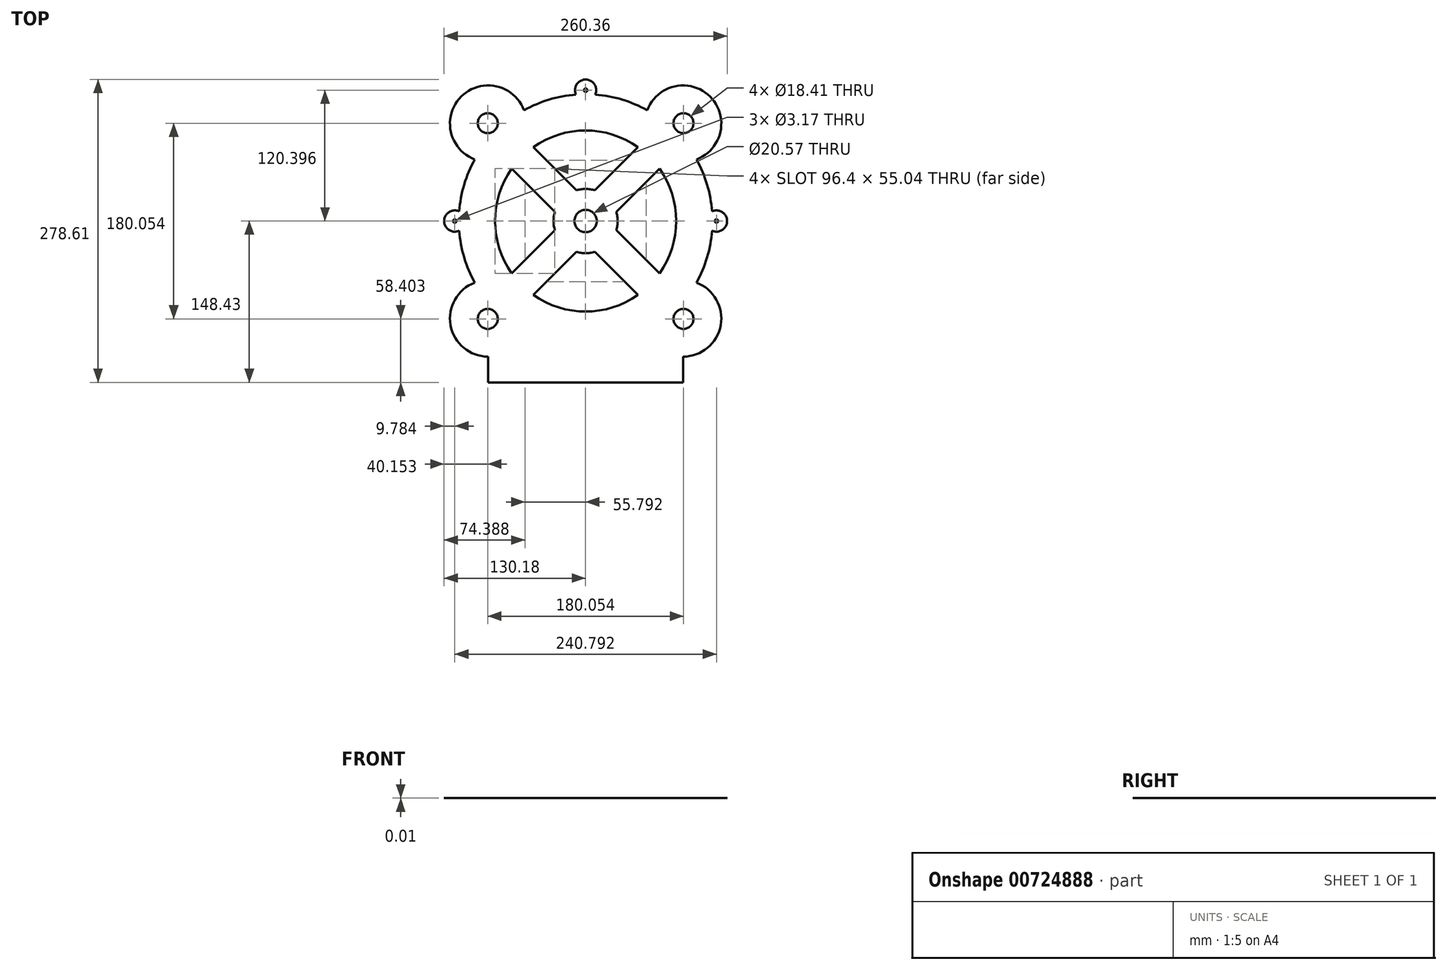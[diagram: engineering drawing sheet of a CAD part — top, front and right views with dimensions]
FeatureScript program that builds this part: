
annotation { "Feature Type Name" : "Feature", "Feature Type Description" : "" }
export const myFeature = defineFeature(function(context is Context, id is Id, definition is map)
    precondition{}
    {
        {
            var Q0;
            Q0=qCreatedBy(makeId("Top.planeOp"),FACE);
            var sketch = newSketch(context, id + "F0", { "sketchPlane" : qUnion([Q0])});
            skCircle(sketch, "E0", {"center": v(0, 0) * mm, "radius": 116.68 * mm});
            skLineSegment(sketch, "E1", {"start": v(0, 0) * mm, "end": v(-122.35, 122.35) * mm});
            skLineSegment(sketch, "E2", {"start": v(0, 0) * mm, "end": v(131.34, 131.34) * mm});
            skLineSegment(sketch, "E3", {"start": v(0, 0) * mm, "end": v(155.82, -155.82) * mm});
            skLineSegment(sketch, "E4", {"start": v(0, 0) * mm, "end": v(-127.24, -127.24) * mm});
            skCircle(sketch, "E5", {"center": v(89.62, 89.62) * mm, "radius": 35.18 * mm});
            skCircle(sketch, "E6", {"center": v(-89.62, -89.62) * mm, "radius": 35.18 * mm});
            skCircle(sketch, "E7", {"center": v(89.62, -89.62) * mm, "radius": 35.18 * mm});
            skCircle(sketch, "E8", {"center": v(-89.62, 89.62) * mm, "radius": 35.18 * mm});
            skCircle(sketch, "E9", {"center": v(0, 120.4) * mm, "radius": 9.78 * mm});
            skCircle(sketch, "E10", {"center": v(120.4, 0) * mm, "radius": 9.78 * mm});
            skCircle(sketch, "E11", {"center": v(-120.4, 0) * mm, "radius": 9.78 * mm});
            skCircle(sketch, "E12", {"center": v(0, 0) * mm, "radius": 10.29 * mm});
            skCircle(sketch, "E13", {"center": v(0, 0) * mm, "radius": 29.53 * mm});
            skCircle(sketch, "E14", {"center": v(-90.03, 90.03) * mm, "radius": 9.2 * mm});
            skCircle(sketch, "E15", {"center": v(90.03, 90.03) * mm, "radius": 9.2 * mm});
            skCircle(sketch, "E16", {"center": v(90.03, -90.03) * mm, "radius": 9.2 * mm});
            skCircle(sketch, "E17", {"center": v(-90.03, -90.03) * mm, "radius": 9.2 * mm});
            skLineSegment(sketch, "E18.0", {"start": v(9.88, 9.88) * mm, "end": v(-48.2, 67.95) * mm});
            skLineSegment(sketch, "E18.1", {"start": v(9.88, 9.88) * mm, "end": v(67.95, -48.2) * mm});
            skLineSegment(sketch, "E19.0", {"start": v(-9.88, -9.88) * mm, "end": v(48.2, -67.95) * mm});
            skLineSegment(sketch, "E19.1", {"start": v(-9.88, -9.88) * mm, "end": v(-67.95, 48.2) * mm});
            skLineSegment(sketch, "E20", {"start": v(-67.95, -48.2) * mm, "end": v(48.2, 67.95) * mm});
            skCircle(sketch, "E21", {"center": v(0, 0) * mm, "radius": 83.31 * mm});
            skLineSegment(sketch, "E22.trimOffspring", {"start": v(-48.2, -67.95) * mm, "end": v(67.95, 48.2) * mm});
            skLineSegment(sketch, "E23", {"start": v(-89.62, -124.8) * mm, "end": v(-89.62, -148.43) * mm});
            skLineSegment(sketch, "E24", {"start": v(-89.62, -148.43) * mm, "end": v(89.62, -148.43) * mm});
            skLineSegment(sketch, "E25", {"start": v(89.62, -148.43) * mm, "end": v(89.62, -124.8) * mm});
            skCircle(sketch, "E26", {"center": v(120.4, 0) * mm, "radius": 1.59 * mm});
            skCircle(sketch, "E27", {"center": v(-120.4, 0) * mm, "radius": 1.59 * mm});
            skCircle(sketch, "E28", {"center": v(0, 120.4) * mm, "radius": 1.59 * mm});
            skSolve(sketch);
        }
        {
            var Q0;
            {var subQ0=sQuery(id+"F0.wireOp",EDGE,"E8");var subQ5=sQuery(id+"F0.wireOp",EDGE,"E0");var subQ6=makeQuery(id+"F0.imprint","INTERSECT",VERTEX,{"disambiguationData":[OD(1.0)],"derivedFrom":[subQ5,subQ0]});Q0=makeQuery(id+"F0.imprint","IMPRINT",FACE,{"disambiguationData":[TD([[makeQuery(id+"F0.imprint","IMPRINT",EDGE,{"disambiguationData":[TD([[subQ6,1.0]])],"derivedFrom":subQ5}),-1.0]])]});}
            var Q1;
            {var subQ0=sQuery(id+"F0.wireOp",EDGE,"E8");var subQ3=sQuery(id+"F0.wireOp",EDGE,"E0");var subQ4=makeQuery(id+"F0.imprint","INTERSECT",VERTEX,{"disambiguationData":[OD(0.0)],"derivedFrom":[subQ3,subQ0]});Q1=makeQuery(id+"F0.imprint","IMPRINT",FACE,{"disambiguationData":[TD([[makeQuery(id+"F0.imprint","IMPRINT",EDGE,{"disambiguationData":[TD([[subQ4,-1.0]])],"derivedFrom":subQ3}),-1.0]])]});}
            var Q2;
            {var subQ0=sQuery(id+"F0.wireOp",EDGE,"E8");var subQ1=sQuery(id+"F0.wireOp",EDGE,"E0");var subQ2=makeQuery(id+"F0.imprint","INTERSECT",VERTEX,{"disambiguationData":[OD(0.0)],"derivedFrom":[subQ1,subQ0]});Q2=makeQuery(id+"F0.imprint","IMPRINT",FACE,{"disambiguationData":[TD([[makeQuery(id+"F0.imprint","IMPRINT",EDGE,{"disambiguationData":[TD([[subQ2,-1.0]])],"derivedFrom":subQ1}),1.0]])]});}
            var Q3;
            {var subQ0=sQuery(id+"F0.wireOp",EDGE,"E8");var subQ1=sQuery(id+"F0.wireOp",EDGE,"E0");var subQ2=makeQuery(id+"F0.imprint","INTERSECT",VERTEX,{"disambiguationData":[OD(1.0)],"derivedFrom":[subQ1,subQ0]});Q3=makeQuery(id+"F0.imprint","IMPRINT",FACE,{"disambiguationData":[TD([[makeQuery(id+"F0.imprint","IMPRINT",EDGE,{"disambiguationData":[TD([[subQ2,1.0]])],"derivedFrom":subQ1}),1.0]])]});}
            var Q4;
            {var subQ8=sQuery(id+"F0.wireOp",EDGE,"E8");var subQ11=sQuery(id+"F0.wireOp",EDGE,"E0");var subQ15=makeQuery(id+"F0.imprint","INTERSECT",VERTEX,{"disambiguationData":[OD(1.0)],"derivedFrom":[subQ11,subQ8]});Q4=makeQuery(id+"F0.imprint","IMPRINT",FACE,{"disambiguationData":[TD([[makeQuery(id+"F0.imprint","IMPRINT",EDGE,{"disambiguationData":[TD([[subQ15,-1.0]])],"derivedFrom":subQ11}),1.0]])]});}
            var Q5;
            {var subQ3=sQuery(id+"F0.wireOp",EDGE,"E5");var subQ9=sQuery(id+"F0.wireOp",EDGE,"E0");var subQ10=makeQuery(id+"F0.imprint","INTERSECT",VERTEX,{"disambiguationData":[OD(1.0)],"derivedFrom":[subQ9,subQ3]});Q5=makeQuery(id+"F0.imprint","IMPRINT",FACE,{"disambiguationData":[TD([[makeQuery(id+"F0.imprint","IMPRINT",EDGE,{"disambiguationData":[TD([[subQ10,-1.0]])],"derivedFrom":subQ9}),1.0]])]});}
            var Q6;
            {var subQ3=sQuery(id+"F0.wireOp",EDGE,"E5");var subQ9=sQuery(id+"F0.wireOp",EDGE,"E0");var subQ14=makeQuery(id+"F0.imprint","INTERSECT",VERTEX,{"disambiguationData":[OD(0.0)],"derivedFrom":[subQ9,subQ3]});Q6=makeQuery(id+"F0.imprint","IMPRINT",FACE,{"disambiguationData":[TD([[makeQuery(id+"F0.imprint","IMPRINT",EDGE,{"disambiguationData":[TD([[subQ14,1.0]])],"derivedFrom":subQ9}),1.0]])]});}
            var Q7;
            {var subQ0=sQuery(id+"F0.wireOp",EDGE,"E6");var subQ1=sQuery(id+"F0.wireOp",EDGE,"E0");var subQ2=makeQuery(id+"F0.imprint","INTERSECT",VERTEX,{"disambiguationData":[OD(1.0)],"derivedFrom":[subQ1,subQ0]});Q7=makeQuery(id+"F0.imprint","IMPRINT",FACE,{"disambiguationData":[TD([[makeQuery(id+"F0.imprint","IMPRINT",EDGE,{"disambiguationData":[TD([[subQ2,-1.0]])],"derivedFrom":subQ1}),1.0]])]});}
            var Q8;
            {var subQ0=sQuery(id+"F0.wireOp",EDGE,"E4");var subQ1=sQuery(id+"F0.wireOp",EDGE,"E0");var subQ2=makeQuery(id+"F0.imprint","INTERSECT",VERTEX,{"derivedFrom":[subQ1,subQ0]});Q8=makeQuery(id+"F0.imprint","IMPRINT",FACE,{"disambiguationData":[TD([[makeQuery(id+"F0.imprint","IMPRINT",EDGE,{"disambiguationData":[TD([[subQ2,-1.0]])],"derivedFrom":subQ1}),1.0]])]});}
            var Q9;
            {var subQ0=sQuery(id+"F0.wireOp",EDGE,"E6");var subQ1=sQuery(id+"F0.wireOp",EDGE,"E0");var subQ2=makeQuery(id+"F0.imprint","INTERSECT",VERTEX,{"disambiguationData":[OD(0.0)],"derivedFrom":[subQ1,subQ0]});Q9=makeQuery(id+"F0.imprint","IMPRINT",FACE,{"disambiguationData":[TD([[makeQuery(id+"F0.imprint","IMPRINT",EDGE,{"disambiguationData":[TD([[subQ2,-1.0]])],"derivedFrom":subQ1}),1.0]])]});}
            var Q10;
            {var subQ0=sQuery(id+"F0.wireOp",EDGE,"E7");var subQ1=sQuery(id+"F0.wireOp",EDGE,"E0");var subQ2=makeQuery(id+"F0.imprint","INTERSECT",VERTEX,{"disambiguationData":[OD(1.0)],"derivedFrom":[subQ1,subQ0]});Q10=makeQuery(id+"F0.imprint","IMPRINT",FACE,{"disambiguationData":[TD([[makeQuery(id+"F0.imprint","IMPRINT",EDGE,{"disambiguationData":[TD([[subQ2,-1.0]])],"derivedFrom":subQ1}),1.0]])]});}
            var Q11;
            {var subQ0=sQuery(id+"F0.wireOp",EDGE,"E7");var subQ1=sQuery(id+"F0.wireOp",EDGE,"E0");var subQ2=makeQuery(id+"F0.imprint","INTERSECT",VERTEX,{"disambiguationData":[OD(0.0)],"derivedFrom":[subQ1,subQ0]});Q11=makeQuery(id+"F0.imprint","IMPRINT",FACE,{"disambiguationData":[TD([[makeQuery(id+"F0.imprint","IMPRINT",EDGE,{"disambiguationData":[TD([[subQ2,1.0]])],"derivedFrom":subQ1}),1.0]])]});}
            var Q12;
            {var subQ0=sQuery(id+"F0.wireOp",EDGE,"E5");var subQ1=sQuery(id+"F0.wireOp",EDGE,"E0");var subQ2=makeQuery(id+"F0.imprint","INTERSECT",VERTEX,{"disambiguationData":[OD(0.0)],"derivedFrom":[subQ1,subQ0]});Q12=makeQuery(id+"F0.imprint","IMPRINT",FACE,{"disambiguationData":[TD([[makeQuery(id+"F0.imprint","IMPRINT",EDGE,{"disambiguationData":[TD([[subQ2,-1.0]])],"derivedFrom":subQ1}),1.0]])]});}
            var Q13;
            {var subQ0=sQuery(id+"F0.wireOp",EDGE,"E5");var subQ1=sQuery(id+"F0.wireOp",EDGE,"E0");var subQ2=makeQuery(id+"F0.imprint","INTERSECT",VERTEX,{"disambiguationData":[OD(1.0)],"derivedFrom":[subQ1,subQ0]});Q13=makeQuery(id+"F0.imprint","IMPRINT",FACE,{"disambiguationData":[TD([[makeQuery(id+"F0.imprint","IMPRINT",EDGE,{"disambiguationData":[TD([[subQ2,1.0]])],"derivedFrom":subQ1}),1.0]])]});}
            var Q14;
            {var subQ0=sQuery(id+"F0.wireOp",EDGE,"E5");var subQ3=sQuery(id+"F0.wireOp",EDGE,"E0");var subQ4=makeQuery(id+"F0.imprint","INTERSECT",VERTEX,{"disambiguationData":[OD(0.0)],"derivedFrom":[subQ3,subQ0]});Q14=makeQuery(id+"F0.imprint","IMPRINT",FACE,{"disambiguationData":[TD([[makeQuery(id+"F0.imprint","IMPRINT",EDGE,{"disambiguationData":[TD([[subQ4,-1.0]])],"derivedFrom":subQ3}),-1.0]])]});}
            var Q15;
            {var subQ0=sQuery(id+"F0.wireOp",EDGE,"E5");var subQ3=sQuery(id+"F0.wireOp",EDGE,"E0");var subQ4=makeQuery(id+"F0.imprint","INTERSECT",VERTEX,{"disambiguationData":[OD(1.0)],"derivedFrom":[subQ3,subQ0]});Q15=makeQuery(id+"F0.imprint","IMPRINT",FACE,{"disambiguationData":[TD([[makeQuery(id+"F0.imprint","IMPRINT",EDGE,{"disambiguationData":[TD([[subQ4,1.0]])],"derivedFrom":subQ3}),-1.0]])]});}
            var Q16;
            {var subQ0=sQuery(id+"F0.wireOp",EDGE,"E6");var subQ3=sQuery(id+"F0.wireOp",EDGE,"E0");var subQ4=makeQuery(id+"F0.imprint","INTERSECT",VERTEX,{"disambiguationData":[OD(0.0)],"derivedFrom":[subQ3,subQ0]});Q16=makeQuery(id+"F0.imprint","IMPRINT",FACE,{"disambiguationData":[TD([[makeQuery(id+"F0.imprint","IMPRINT",EDGE,{"disambiguationData":[TD([[subQ4,-1.0]])],"derivedFrom":subQ3}),-1.0]])]});}
            var Q17;
            {var subQ2=sQuery(id+"F0.wireOp",EDGE,"E4");var subQ6=sQuery(id+"F0.wireOp",EDGE,"E0");var subQ7=makeQuery(id+"F0.imprint","INTERSECT",VERTEX,{"derivedFrom":[subQ6,subQ2]});Q17=makeQuery(id+"F0.imprint","IMPRINT",FACE,{"disambiguationData":[TD([[makeQuery(id+"F0.imprint","IMPRINT",EDGE,{"disambiguationData":[TD([[subQ7,-1.0]])],"derivedFrom":subQ6}),-1.0]])]});}
            var Q18;
            {var subQ0=sQuery(id+"F0.wireOp",EDGE,"E7");var subQ2=sQuery(id+"F0.wireOp",EDGE,"E0");var subQ3=makeQuery(id+"F0.imprint","INTERSECT",VERTEX,{"disambiguationData":[OD(1.0)],"derivedFrom":[subQ2,subQ0]});Q18=makeQuery(id+"F0.imprint","IMPRINT",FACE,{"disambiguationData":[TD([[makeQuery(id+"F0.imprint","IMPRINT",EDGE,{"disambiguationData":[TD([[subQ3,-1.0]])],"derivedFrom":subQ2}),-1.0]])]});}
            var Q19;
            {var subQ0=sQuery(id+"F0.wireOp",EDGE,"E7");var subQ6=sQuery(id+"F0.wireOp",EDGE,"E0");var subQ7=makeQuery(id+"F0.imprint","INTERSECT",VERTEX,{"disambiguationData":[OD(0.0)],"derivedFrom":[subQ6,subQ0]});Q19=makeQuery(id+"F0.imprint","IMPRINT",FACE,{"disambiguationData":[TD([[makeQuery(id+"F0.imprint","IMPRINT",EDGE,{"disambiguationData":[TD([[subQ7,1.0]])],"derivedFrom":subQ6}),-1.0]])]});}
            var Q20;
            Q20=makeQuery(id+"F0.imprint","IMPRINT",FACE,{"disambiguationData":[TD([[makeQuery(id+"F0.imprint","IMPRINT",EDGE,{"derivedFrom":sQuery(id+"F0.wireOp",EDGE,"E26")}),-1.0]])]});
            var Q21;
            {var subQ0=sQuery(id+"F0.wireOp",EDGE,"E10");var subQ1=sQuery(id+"F0.wireOp",EDGE,"E0");var subQ2=makeQuery(id+"F0.imprint","INTERSECT",VERTEX,{"disambiguationData":[OD(0.0)],"derivedFrom":[subQ1,subQ0]});Q21=makeQuery(id+"F0.imprint","IMPRINT",FACE,{"disambiguationData":[TD([[makeQuery(id+"F0.imprint","IMPRINT",EDGE,{"disambiguationData":[TD([[subQ2,1.0]])],"derivedFrom":subQ1}),1.0]])]});}
            var Q22;
            {var subQ0=sQuery(id+"F0.wireOp",EDGE,"E11");var subQ1=sQuery(id+"F0.wireOp",EDGE,"E0");var subQ2=makeQuery(id+"F0.imprint","INTERSECT",VERTEX,{"disambiguationData":[OD(0.0)],"derivedFrom":[subQ1,subQ0]});Q22=makeQuery(id+"F0.imprint","IMPRINT",FACE,{"disambiguationData":[TD([[makeQuery(id+"F0.imprint","IMPRINT",EDGE,{"disambiguationData":[TD([[subQ2,-1.0]])],"derivedFrom":subQ1}),1.0]])]});}
            var Q23;
            Q23=makeQuery(id+"F0.imprint","IMPRINT",FACE,{"disambiguationData":[TD([[makeQuery(id+"F0.imprint","IMPRINT",EDGE,{"derivedFrom":sQuery(id+"F0.wireOp",EDGE,"E27")}),-1.0]])]});
            var Q24;
            {var subQ0=sQuery(id+"F0.wireOp",EDGE,"E9");var subQ1=sQuery(id+"F0.wireOp",EDGE,"E0");var subQ2=makeQuery(id+"F0.imprint","INTERSECT",VERTEX,{"disambiguationData":[OD(0.0)],"derivedFrom":[subQ1,subQ0]});Q24=makeQuery(id+"F0.imprint","IMPRINT",FACE,{"disambiguationData":[TD([[makeQuery(id+"F0.imprint","IMPRINT",EDGE,{"disambiguationData":[TD([[subQ2,-1.0]])],"derivedFrom":subQ1}),1.0]])]});}
            var Q25;
            Q25=makeQuery(id+"F0.imprint","IMPRINT",FACE,{"disambiguationData":[TD([[makeQuery(id+"F0.imprint","IMPRINT",EDGE,{"derivedFrom":sQuery(id+"F0.wireOp",EDGE,"E28")}),-1.0]])]});
            var Q26;
            {var subQ4=sQuery(id+"F0.wireOp",EDGE,"E23");Q26=makeQuery(id+"F0.imprint","IMPRINT",FACE,{"disambiguationData":[TD([[makeQuery(id+"F0.imprint","IMPRINT",EDGE,{"derivedFrom":subQ4}),1.0]])]});}
            var Q27;
            {var subQ0=sQuery(id+"F0.wireOp",EDGE,"E13");var subQ1=sQuery(id+"F0.wireOp",EDGE,"E3");var subQ2=makeQuery(id+"F0.imprint","INTERSECT",VERTEX,{"derivedFrom":[subQ1,subQ0]});Q27=makeQuery(id+"F0.imprint","IMPRINT",FACE,{"disambiguationData":[TD([[makeQuery(id+"F0.imprint","IMPRINT",EDGE,{"disambiguationData":[TD([[subQ2,-1.0]])],"derivedFrom":subQ1}),-1.0]])]});}
            var Q28;
            {var subQ0=sQuery(id+"F0.wireOp",EDGE,"E13");var subQ1=sQuery(id+"F0.wireOp",EDGE,"E3");var subQ2=makeQuery(id+"F0.imprint","INTERSECT",VERTEX,{"derivedFrom":[subQ1,subQ0]});Q28=makeQuery(id+"F0.imprint","IMPRINT",FACE,{"disambiguationData":[TD([[makeQuery(id+"F0.imprint","IMPRINT",EDGE,{"disambiguationData":[TD([[subQ2,-1.0]])],"derivedFrom":subQ1}),1.0]])]});}
            var Q29;
            {var subQ0=sQuery(id+"F0.wireOp",EDGE,"E22.trimOffspring");var subQ1=sQuery(id+"F0.wireOp",EDGE,"E3");var subQ2=makeQuery(id+"F0.imprint","INTERSECT",VERTEX,{"derivedFrom":[subQ1,subQ0]});Q29=makeQuery(id+"F0.imprint","IMPRINT",FACE,{"disambiguationData":[TD([[makeQuery(id+"F0.imprint","IMPRINT",EDGE,{"disambiguationData":[TD([[subQ2,-1.0]])],"derivedFrom":subQ1}),1.0]])]});}
            var Q30;
            {var subQ0=sQuery(id+"F0.wireOp",EDGE,"E22.trimOffspring");var subQ1=sQuery(id+"F0.wireOp",EDGE,"E3");var subQ2=makeQuery(id+"F0.imprint","INTERSECT",VERTEX,{"derivedFrom":[subQ1,subQ0]});Q30=makeQuery(id+"F0.imprint","IMPRINT",FACE,{"disambiguationData":[TD([[makeQuery(id+"F0.imprint","IMPRINT",EDGE,{"disambiguationData":[TD([[subQ2,-1.0]])],"derivedFrom":subQ1}),-1.0]])]});}
            var Q31;
            {var subQ1=sQuery(id+"F0.wireOp",EDGE,"E4");var subQ3=sQuery(id+"F0.wireOp",EDGE,"E13");var subQ4=makeQuery(id+"F0.imprint","INTERSECT",VERTEX,{"derivedFrom":[subQ1,subQ3]});Q31=makeQuery(id+"F0.imprint","IMPRINT",FACE,{"disambiguationData":[TD([[makeQuery(id+"F0.imprint","IMPRINT",EDGE,{"disambiguationData":[TD([[subQ4,-1.0]])],"derivedFrom":subQ3}),1.0]])]});}
            var Q32;
            {var subQ0=sQuery(id+"F0.wireOp",EDGE,"E13");var subQ1=sQuery(id+"F0.wireOp",EDGE,"E4");var subQ2=makeQuery(id+"F0.imprint","INTERSECT",VERTEX,{"derivedFrom":[subQ1,subQ0]});Q32=makeQuery(id+"F0.imprint","IMPRINT",FACE,{"disambiguationData":[TD([[makeQuery(id+"F0.imprint","IMPRINT",EDGE,{"disambiguationData":[TD([[subQ2,-1.0]])],"derivedFrom":subQ1}),1.0]])]});}
            var Q33;
            {var subQ0=sQuery(id+"F0.wireOp",EDGE,"E13");var subQ1=sQuery(id+"F0.wireOp",EDGE,"E4");var subQ2=makeQuery(id+"F0.imprint","INTERSECT",VERTEX,{"derivedFrom":[subQ1,subQ0]});Q33=makeQuery(id+"F0.imprint","IMPRINT",FACE,{"disambiguationData":[TD([[makeQuery(id+"F0.imprint","IMPRINT",EDGE,{"disambiguationData":[TD([[subQ2,-1.0]])],"derivedFrom":subQ1}),-1.0]])]});}
            var Q34;
            {var subQ0=sQuery(id+"F0.wireOp",EDGE,"E22.trimOffspring");var subQ1=sQuery(id+"F0.wireOp",EDGE,"E13");var subQ2=makeQuery(id+"F0.imprint","INTERSECT",VERTEX,{"disambiguationData":[OD(1.0)],"derivedFrom":[subQ1,subQ0]});Q34=makeQuery(id+"F0.imprint","IMPRINT",FACE,{"disambiguationData":[TD([[makeQuery(id+"F0.imprint","IMPRINT",EDGE,{"disambiguationData":[TD([[subQ2,-1.0]])],"derivedFrom":subQ1}),1.0]])]});}
            var Q35;
            {var subQ0=sQuery(id+"F0.wireOp",EDGE,"E22.trimOffspring");var subQ1=sQuery(id+"F0.wireOp",EDGE,"E13");var subQ2=makeQuery(id+"F0.imprint","INTERSECT",VERTEX,{"disambiguationData":[OD(0.0)],"derivedFrom":[subQ1,subQ0]});Q35=makeQuery(id+"F0.imprint","IMPRINT",FACE,{"disambiguationData":[TD([[makeQuery(id+"F0.imprint","IMPRINT",EDGE,{"disambiguationData":[TD([[subQ2,1.0]])],"derivedFrom":subQ1}),1.0]])]});}
            var Q36;
            {var subQ1=sQuery(id+"F0.wireOp",EDGE,"E4");var subQ3=sQuery(id+"F0.wireOp",EDGE,"E13");var subQ4=makeQuery(id+"F0.imprint","INTERSECT",VERTEX,{"derivedFrom":[subQ1,subQ3]});Q36=makeQuery(id+"F0.imprint","IMPRINT",FACE,{"disambiguationData":[TD([[makeQuery(id+"F0.imprint","IMPRINT",EDGE,{"disambiguationData":[TD([[subQ4,1.0]])],"derivedFrom":subQ3}),1.0]])]});}
            var Q37;
            {var subQ0=sQuery(id+"F0.wireOp",EDGE,"E19.1");var subQ1=sQuery(id+"F0.wireOp",EDGE,"E13");var subQ2=makeQuery(id+"F0.imprint","INTERSECT",VERTEX,{"derivedFrom":[subQ1,subQ0]});Q37=makeQuery(id+"F0.imprint","IMPRINT",FACE,{"disambiguationData":[TD([[makeQuery(id+"F0.imprint","IMPRINT",EDGE,{"disambiguationData":[TD([[subQ2,-1.0]])],"derivedFrom":subQ1}),1.0]])]});}
            var Q38;
            {var subQ0=sQuery(id+"F0.wireOp",EDGE,"E20");var subQ1=sQuery(id+"F0.wireOp",EDGE,"E1");var subQ2=makeQuery(id+"F0.imprint","INTERSECT",VERTEX,{"derivedFrom":[subQ1,subQ0]});Q38=makeQuery(id+"F0.imprint","IMPRINT",FACE,{"disambiguationData":[TD([[makeQuery(id+"F0.imprint","IMPRINT",EDGE,{"disambiguationData":[TD([[subQ2,-1.0]])],"derivedFrom":subQ1}),1.0]])]});}
            var Q39;
            {var subQ0=sQuery(id+"F0.wireOp",EDGE,"E20");var subQ1=sQuery(id+"F0.wireOp",EDGE,"E1");var subQ2=makeQuery(id+"F0.imprint","INTERSECT",VERTEX,{"derivedFrom":[subQ1,subQ0]});Q39=makeQuery(id+"F0.imprint","IMPRINT",FACE,{"disambiguationData":[TD([[makeQuery(id+"F0.imprint","IMPRINT",EDGE,{"disambiguationData":[TD([[subQ2,-1.0]])],"derivedFrom":subQ1}),-1.0]])]});}
            var Q40;
            {var subQ0=sQuery(id+"F0.wireOp",EDGE,"E20");var subQ1=sQuery(id+"F0.wireOp",EDGE,"E13");var subQ2=makeQuery(id+"F0.imprint","INTERSECT",VERTEX,{"disambiguationData":[OD(0.0)],"derivedFrom":[subQ1,subQ0]});Q40=makeQuery(id+"F0.imprint","IMPRINT",FACE,{"disambiguationData":[TD([[makeQuery(id+"F0.imprint","IMPRINT",EDGE,{"disambiguationData":[TD([[subQ2,-1.0]])],"derivedFrom":subQ1}),1.0]])]});}
            var Q41;
            {var subQ1=sQuery(id+"F0.wireOp",EDGE,"E2");var subQ3=sQuery(id+"F0.wireOp",EDGE,"E13");var subQ4=makeQuery(id+"F0.imprint","INTERSECT",VERTEX,{"derivedFrom":[subQ1,subQ3]});Q41=makeQuery(id+"F0.imprint","IMPRINT",FACE,{"disambiguationData":[TD([[makeQuery(id+"F0.imprint","IMPRINT",EDGE,{"disambiguationData":[TD([[subQ4,-1.0]])],"derivedFrom":subQ3}),1.0]])]});}
            var Q42;
            {var subQ1=sQuery(id+"F0.wireOp",EDGE,"E2");var subQ3=sQuery(id+"F0.wireOp",EDGE,"E13");var subQ4=makeQuery(id+"F0.imprint","INTERSECT",VERTEX,{"derivedFrom":[subQ1,subQ3]});Q42=makeQuery(id+"F0.imprint","IMPRINT",FACE,{"disambiguationData":[TD([[makeQuery(id+"F0.imprint","IMPRINT",EDGE,{"disambiguationData":[TD([[subQ4,1.0]])],"derivedFrom":subQ3}),1.0]])]});}
            var Q43;
            {var subQ5=sQuery(id+"F0.wireOp",EDGE,"E12");var subQ7=sQuery(id+"F0.wireOp",EDGE,"E3");var subQ8=makeQuery(id+"F0.imprint","INTERSECT",VERTEX,{"derivedFrom":[subQ7,subQ5]});Q43=makeQuery(id+"F0.imprint","IMPRINT",FACE,{"disambiguationData":[TD([[makeQuery(id+"F0.imprint","IMPRINT",EDGE,{"disambiguationData":[TD([[subQ8,-1.0]])],"derivedFrom":subQ7}),1.0]])]});}
            var Q44;
            {var subQ5=sQuery(id+"F0.wireOp",EDGE,"E12");var subQ6=sQuery(id+"F0.wireOp",EDGE,"E3");var subQ7=makeQuery(id+"F0.imprint","INTERSECT",VERTEX,{"derivedFrom":[subQ6,subQ5]});Q44=makeQuery(id+"F0.imprint","IMPRINT",FACE,{"disambiguationData":[TD([[makeQuery(id+"F0.imprint","IMPRINT",EDGE,{"disambiguationData":[TD([[subQ7,-1.0]])],"derivedFrom":subQ6}),-1.0]])]});}
            var Q45;
            {var subQ5=sQuery(id+"F0.wireOp",EDGE,"E12");var subQ7=sQuery(id+"F0.wireOp",EDGE,"E1");var subQ8=makeQuery(id+"F0.imprint","INTERSECT",VERTEX,{"derivedFrom":[subQ7,subQ5]});Q45=makeQuery(id+"F0.imprint","IMPRINT",FACE,{"disambiguationData":[TD([[makeQuery(id+"F0.imprint","IMPRINT",EDGE,{"disambiguationData":[TD([[subQ8,-1.0]])],"derivedFrom":subQ7}),1.0]])]});}
            var Q46;
            {var subQ5=sQuery(id+"F0.wireOp",EDGE,"E12");var subQ6=sQuery(id+"F0.wireOp",EDGE,"E1");var subQ7=makeQuery(id+"F0.imprint","INTERSECT",VERTEX,{"derivedFrom":[subQ6,subQ5]});Q46=makeQuery(id+"F0.imprint","IMPRINT",FACE,{"disambiguationData":[TD([[makeQuery(id+"F0.imprint","IMPRINT",EDGE,{"disambiguationData":[TD([[subQ7,-1.0]])],"derivedFrom":subQ6}),-1.0]])]});}
            var Q47;
            {var subQ0=sQuery(id+"F0.wireOp",EDGE,"E13");var subQ1=sQuery(id+"F0.wireOp",EDGE,"E2");var subQ2=makeQuery(id+"F0.imprint","INTERSECT",VERTEX,{"derivedFrom":[subQ1,subQ0]});Q47=makeQuery(id+"F0.imprint","IMPRINT",FACE,{"disambiguationData":[TD([[makeQuery(id+"F0.imprint","IMPRINT",EDGE,{"disambiguationData":[TD([[subQ2,-1.0]])],"derivedFrom":subQ1}),-1.0]])]});}
            var Q48;
            {var subQ0=sQuery(id+"F0.wireOp",EDGE,"E13");var subQ1=sQuery(id+"F0.wireOp",EDGE,"E2");var subQ2=makeQuery(id+"F0.imprint","INTERSECT",VERTEX,{"derivedFrom":[subQ1,subQ0]});Q48=makeQuery(id+"F0.imprint","IMPRINT",FACE,{"disambiguationData":[TD([[makeQuery(id+"F0.imprint","IMPRINT",EDGE,{"disambiguationData":[TD([[subQ2,-1.0]])],"derivedFrom":subQ1}),1.0]])]});}
            var Q49;
            {var subQ0=sQuery(id+"F0.wireOp",EDGE,"E13");var subQ1=sQuery(id+"F0.wireOp",EDGE,"E1");var subQ2=makeQuery(id+"F0.imprint","INTERSECT",VERTEX,{"derivedFrom":[subQ1,subQ0]});Q49=makeQuery(id+"F0.imprint","IMPRINT",FACE,{"disambiguationData":[TD([[makeQuery(id+"F0.imprint","IMPRINT",EDGE,{"disambiguationData":[TD([[subQ2,-1.0]])],"derivedFrom":subQ1}),-1.0]])]});}
            var Q50;
            {var subQ0=sQuery(id+"F0.wireOp",EDGE,"E13");var subQ1=sQuery(id+"F0.wireOp",EDGE,"E1");var subQ2=makeQuery(id+"F0.imprint","INTERSECT",VERTEX,{"derivedFrom":[subQ1,subQ0]});Q50=makeQuery(id+"F0.imprint","IMPRINT",FACE,{"disambiguationData":[TD([[makeQuery(id+"F0.imprint","IMPRINT",EDGE,{"disambiguationData":[TD([[subQ2,-1.0]])],"derivedFrom":subQ1}),1.0]])]});}
            extrude(context, id + "F1", {"entities" : qUnion([Q0, Q1, Q2, Q3, Q4, Q5, Q6, Q7, Q8, Q9, Q10, Q11, Q12, Q13, Q14, Q15, Q16, Q17, Q18, Q19, Q20, Q21, Q22, Q23, Q24, Q25, Q26, Q27, Q28, Q29, Q30, Q31, Q32, Q33, Q34, Q35, Q36, Q37, Q38, Q39, Q40, Q41, Q42, Q43, Q44, Q45, Q46, Q47, Q48, Q49, Q50]), "depth" : 3 / 406.4 * mm, "offsetDistance" : 25.4 * mm});
        }
    });
